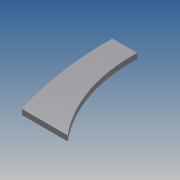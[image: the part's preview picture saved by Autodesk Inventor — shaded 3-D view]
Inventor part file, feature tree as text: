
AUTODESK INVENTOR PART (.ipt)
format: ipt  version: 2015 (Build 190159000, 159)  size: 101,888 bytes
history: native  units: mm
features: extrude x1, sketch x1
ambient origin geometry x8: Origin, YZ Plane, XZ Plane, XY Plane, X Axis, Y Axis, Z Axis, Center Point
bodies: Body1 (feature_tree)
feature tree (2):
  extrude  "Extrusion5"  Depth=40.0mm
  sketch  "Skizze3"  dims[d4=1000.0mm d5=1000.0mm d6=100.0mm d7=550.0mm d8=180.0mm d9=100.0mm d10=100.0mm d11=320.0mm d12=300.0mm d13=350.0mm d14=230.0mm d15=60.0mm d16=-60.0mm d17=130.0mm d18=190.0mm d19=50.0mm d21=283.537414mm d22=40.0mm d23=140.0mm d24=899.502025mm d25=919.104612mm d26=330.793649mm d33=40.0mm d34=0.0mm]
